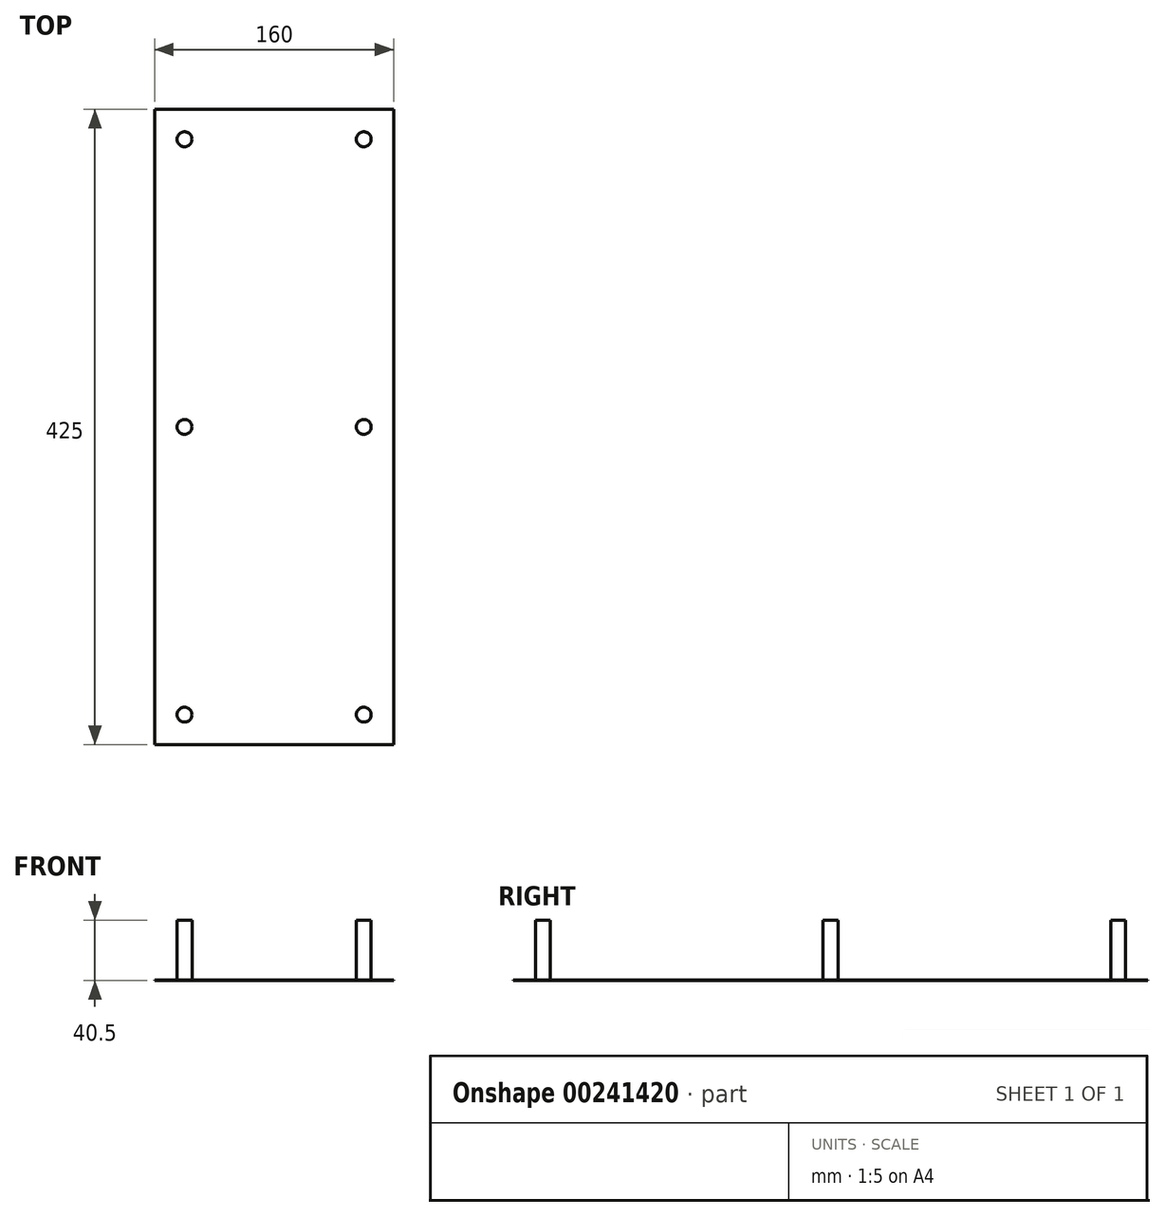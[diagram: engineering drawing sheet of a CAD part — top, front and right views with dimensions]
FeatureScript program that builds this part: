
annotation { "Feature Type Name" : "Feature", "Feature Type Description" : "" }
export const myFeature = defineFeature(function(context is Context, id is Id, definition is map)
    precondition{}
    {
        {
            var Q0;
            Q0=qCreatedBy(makeId("Top.planeOp"),FACE);
            var sketch = newSketch(context, id + "F0", { "sketchPlane" : qUnion([Q0])});
            skLineSegment(sketch, "E0.bottom", {"start": v(-80, 212.5) * mm, "end": v(80, 212.5) * mm});
            skLineSegment(sketch, "E0.top", {"start": v(-80, -212.5) * mm, "end": v(80, -212.5) * mm});
            skLineSegment(sketch, "E0.left", {"start": v(-80, 212.5) * mm, "end": v(-80, -212.5) * mm});
            skLineSegment(sketch, "E0.right", {"start": v(80, 212.5) * mm, "end": v(80, -212.5) * mm});
            skPoint(sketch, "E0.middle", {"position": v(0, 0) * mm});
            skSolve(sketch);
        }
        {
            var Q0;
            Q0 = qSketchRegion(id + "F0", true);
            extrude(context, id + "F1", {"entities" : qUnion([Q0]), "depth" : 0.5 * mm});
        }
        {
            var Q0;
            Q0=makeQuery(id+"F1.opExtrude","CAP_FACE",FACE,{"disambiguationData":[OSD([sQuery(id+"F0.wireOp",EDGE,"E0.bottom"),sQuery(id+"F0.wireOp",EDGE,"E0.top"),sQuery(id+"F0.wireOp",EDGE,"E0.left"),sQuery(id+"F0.wireOp",EDGE,"E0.right")])],"isStart":false});
            var sketch = newSketch(context, id + "F2", { "sketchPlane" : qUnion([Q0])});
            skCircle(sketch, "E1", {"center": v(-60, 192.5) * mm, "radius": 5 * mm});
            skCircle(sketch, "E2", {"center": v(60, 192.5) * mm, "radius": 5 * mm});
            skCircle(sketch, "E3", {"center": v(60, -192.5) * mm, "radius": 5 * mm});
            skCircle(sketch, "E4", {"center": v(-60, -192.5) * mm, "radius": 5 * mm});
            skCircle(sketch, "E5", {"center": v(-60, 0) * mm, "radius": 5 * mm});
            skCircle(sketch, "E6", {"center": v(60, 0) * mm, "radius": 5 * mm});
            skSolve(sketch);
        }
        {
            var Q0;
            Q0 = qSketchRegion(id + "F2", true);
            extrude(context, id + "F3", {"entities" : qUnion([Q0]), "operationType" : NewBodyOperationType.ADD, "depth" : 40 * mm});
        }
    });
